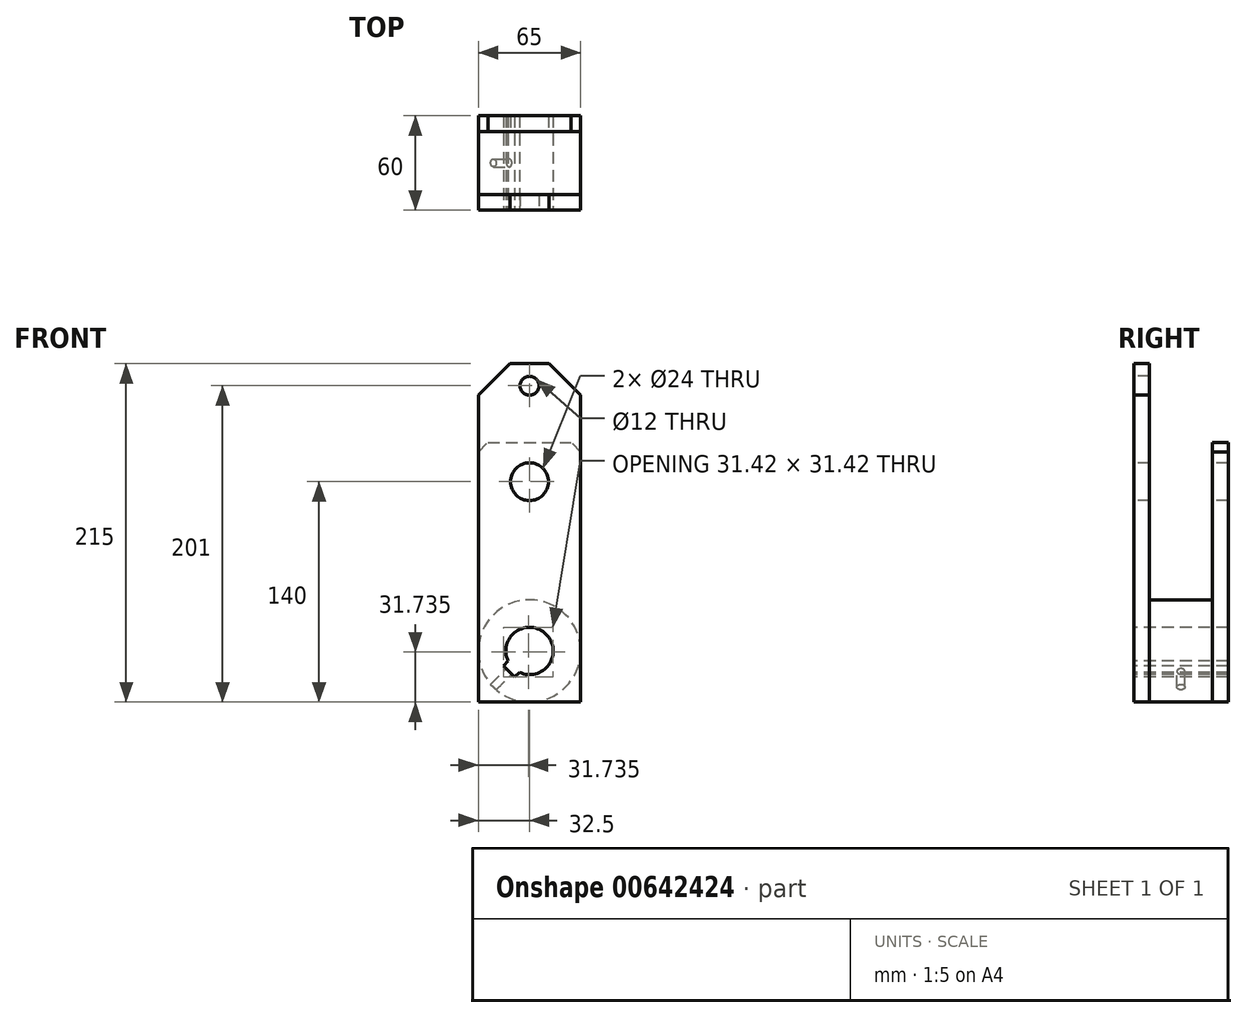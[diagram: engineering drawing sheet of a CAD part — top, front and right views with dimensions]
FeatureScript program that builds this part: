
annotation { "Feature Type Name" : "Feature", "Feature Type Description" : "" }
export const myFeature = defineFeature(function(context is Context, id is Id, definition is map)
    precondition{}
    {
        {
            var Q0;
            Q0=qCreatedBy(makeId("Front.planeOp"),FACE);
            var sketch = newSketch(context, id + "F0", { "sketchPlane" : qUnion([Q0])});
            skLineSegment(sketch, "E0.bottom", {"start": v(32.5, 107.5) * mm, "end": v(-32.5, 107.5) * mm});
            skLineSegment(sketch, "E0.top", {"start": v(32.5, -107.5) * mm, "end": v(-32.5, -107.5) * mm});
            skLineSegment(sketch, "E0.left", {"start": v(32.5, 107.5) * mm, "end": v(32.5, -107.5) * mm});
            skLineSegment(sketch, "E0.right", {"start": v(-32.5, 107.5) * mm, "end": v(-32.5, -107.5) * mm});
            skPoint(sketch, "E0.middle", {"position": v(0, 0) * mm});
            skPoint(sketch, "E1", {"position": v(0, -75) * mm});
            skSolve(sketch);
        }
        {
            var Q0;
            Q0=makeQuery(id+"F0.imprint","IMPRINT",FACE,{"disambiguationData":[TD([[makeQuery(id+"F0.imprint","IMPRINT",EDGE,{"derivedFrom":sQuery(id+"F0.wireOp",EDGE,"E0.bottom")}),1.0]])]});
            extrude(context, id + "F1", {"entities" : qUnion([Q0]), "oppositeDirection" : true, "depth" : 10 * mm, "offsetDistance" : 25 * mm});
        }
        {
            var Q0;
            Q0=makeQuery(id+"F1.opExtrude","SWEPT_EDGE",EDGE,{"disambiguationData":[OSD([sQuery(id+"F0.wireOp",EDGE,"E0.bottom"),sQuery(id+"F0.wireOp",EDGE,"E0.right")])]});
            var Q1;
            Q1=makeQuery(id+"F1.opExtrude","SWEPT_EDGE",EDGE,{"disambiguationData":[OSD([sQuery(id+"F0.wireOp",EDGE,"E0.bottom"),sQuery(id+"F0.wireOp",EDGE,"E0.left")])]});
            chamfer(context, id + "F2", {"entities" : qUnion([Q0, Q1]), "width" : 20 * mm, "tangentPropagation" : true});
        }
        {
            var Q0;
            Q0=makeQuery(id+"F1.opExtrude","CAP_FACE",FACE,{"disambiguationData":[OSD([sQuery(id+"F0.wireOp",EDGE,"E0.bottom"),sQuery(id+"F0.wireOp",EDGE,"E0.top"),sQuery(id+"F0.wireOp",EDGE,"E0.left"),sQuery(id+"F0.wireOp",EDGE,"E0.right")])],"isStart":false});
            var sketch = newSketch(context, id + "F3", { "sketchPlane" : qUnion([Q0])});
            skCircle(sketch, "E2", {"center": v(0, -75) * mm, "radius": 32.5 * mm});
            skSolve(sketch);
        }
        {
            var Q0;
            {var subQ0=sQuery(id+"F3.wireOp",EDGE,"E2");var subQ1=makeQuery(id+"F3.imprint","INTERSECT",VERTEX,{"derivedFrom":[makeQuery(id+"F1.opExtrude","CAP_EDGE",EDGE,{"disambiguationData":[OSD([sQuery(id+"F0.wireOp",EDGE,"E0.left")])],"isStart":false}),subQ0]});Q0=makeQuery(id+"F3.imprint","IMPRINT",FACE,{"disambiguationData":[TD([[makeQuery(id+"F3.imprint","IMPRINT",EDGE,{"disambiguationData":[TD([[subQ1,1.0]])],"derivedFrom":subQ0}),1.0]])]});}
            extrude(context, id + "F4", {"entities" : qUnion([Q0]), "operationType" : NewBodyOperationType.ADD, "depth" : 40 * mm, "offsetDistance" : 25 * mm});
        }
        {
            var Q0;
            Q0=makeQuery(id+"F4.opExtrude","CAP_FACE",FACE,{"disambiguationData":[OSD([sQuery(id+"F3.wireOp",EDGE,"E2")])],"isStart":false});
            var sketch = newSketch(context, id + "F5", { "sketchPlane" : qUnion([Q0])});
            skLineSegment(sketch, "E3.bottom", {"start": v(32.5, -107.5) * mm, "end": v(-32.5, -107.5) * mm});
            skLineSegment(sketch, "E3.top", {"start": v(32.5, 57.5) * mm, "end": v(-32.5, 57.5) * mm});
            skLineSegment(sketch, "E3.left", {"start": v(32.5, -107.5) * mm, "end": v(32.5, 57.5) * mm});
            skLineSegment(sketch, "E3.right", {"start": v(-32.5, -107.5) * mm, "end": v(-32.5, 57.5) * mm});
            skPoint(sketch, "E3.middle", {"position": v(0, -25) * mm});
            skSolve(sketch);
        }
        {
            var Q0;
            {var subQ0=sQuery(id+"F5.wireOp",EDGE,"E3.top");Q0=makeQuery(id+"F5.imprint","IMPRINT",FACE,{"disambiguationData":[TD([[makeQuery(id+"F5.imprint","IMPRINT",EDGE,{"derivedFrom":subQ0}),1.0]])]});}
            var Q1;
            {var subQ0=makeQuery(id+"F4.opExtrude","CAP_EDGE",EDGE,{"disambiguationData":[OSD([sQuery(id+"F3.wireOp",EDGE,"E2")])],"isStart":false});var subQ1=makeQuery(id+"F5.imprint","INTERSECT",VERTEX,{"derivedFrom":[subQ0,sQuery(id+"F5.wireOp",EDGE,"E3.bottom")]});Q1=makeQuery(id+"F5.imprint","IMPRINT",FACE,{"disambiguationData":[TD([[makeQuery(id+"F5.imprint","IMPRINT",EDGE,{"disambiguationData":[TD([[subQ1,-1.0]])],"derivedFrom":subQ0}),1.0]])]});}
            var Q2;
            {var subQ0=sQuery(id+"F5.wireOp",EDGE,"E3.right");var subQ1=sQuery(id+"F5.wireOp",EDGE,"E3.bottom");var subQ2=makeQuery(id+"F5.imprint","INTERSECT",VERTEX,{"derivedFrom":[subQ1,subQ0]});Q2=makeQuery(id+"F5.imprint","IMPRINT",FACE,{"disambiguationData":[TD([[makeQuery(id+"F5.imprint","IMPRINT",EDGE,{"disambiguationData":[TD([[subQ2,1.0]])],"derivedFrom":subQ1}),-1.0]])]});}
            var Q3;
            {var subQ0=sQuery(id+"F5.wireOp",EDGE,"E3.left");var subQ1=sQuery(id+"F5.wireOp",EDGE,"E3.bottom");var subQ2=makeQuery(id+"F5.imprint","INTERSECT",VERTEX,{"derivedFrom":[subQ1,subQ0]});Q3=makeQuery(id+"F5.imprint","IMPRINT",FACE,{"disambiguationData":[TD([[makeQuery(id+"F5.imprint","IMPRINT",EDGE,{"disambiguationData":[TD([[subQ2,-1.0]])],"derivedFrom":subQ1}),-1.0]])]});}
            extrude(context, id + "F6", {"entities" : qUnion([Q0, Q1, Q2, Q3]), "operationType" : NewBodyOperationType.ADD, "depth" : 10 * mm, "offsetDistance" : 25 * mm});
        }
        {
            var Q0;
            Q0=makeQuery(id+"F6.opExtrude","SWEPT_EDGE",EDGE,{"disambiguationData":[OSD([sQuery(id+"F5.wireOp",EDGE,"E3.top"),sQuery(id+"F5.wireOp",EDGE,"E3.right")])]});
            var Q1;
            Q1=makeQuery(id+"F6.opExtrude","SWEPT_EDGE",EDGE,{"disambiguationData":[OSD([sQuery(id+"F5.wireOp",EDGE,"E3.top"),sQuery(id+"F5.wireOp",EDGE,"E3.left")])]});
            chamfer(context, id + "F7", {"entities" : qUnion([Q0, Q1]), "width" : 6 * mm, "tangentPropagation" : true});
        }
        {
            var Q0;
            Q0=makeQuery(id+"F1.opExtrude","CAP_FACE",FACE,{"disambiguationData":[OSD([sQuery(id+"F0.wireOp",EDGE,"E0.bottom"),sQuery(id+"F0.wireOp",EDGE,"E0.top"),sQuery(id+"F0.wireOp",EDGE,"E0.left"),sQuery(id+"F0.wireOp",EDGE,"E0.right")])],"isStart":true});
            var sketch = newSketch(context, id + "F8", { "sketchPlane" : qUnion([Q0])});
            skPoint(sketch, "E4", {"position": v(0, -75) * mm});
            skPoint(sketch, "E5", {"position": v(0, 32.5) * mm});
            skSolve(sketch);
        }
        {
            var Q0;
            Q0=sQuery(id+"F8.wireOp",VERTEX,"E4");
            var Q1;
            Q1=makeQuery(id+"F1.opExtrude","SWEPT_BODY",BODY,{"disambiguationData":[OSD([sQuery(id+"F0.wireOp",EDGE,"E0.bottom"),sQuery(id+"F0.wireOp",EDGE,"E0.top"),sQuery(id+"F0.wireOp",EDGE,"E0.left"),sQuery(id+"F0.wireOp",EDGE,"E0.right")])]});
            hole(context, id + "F9", {"style" : HoleStyle.SIMPLE, "endStyle" : HoleEndStyle.THROUGH, "standardTappedOrClearance" : lookupTablePath({ "standard" : "ISO", "size" : "30", "type" : "Drilled" }), "standardBlindInLast" : lookupTablePath({ "standard" : "ISO", "size" : "30", "type" : "Drilled" }), "holeDiameter" : 30 * mm, "majorDiameter" : 5 * mm, "isTappedThrough" : true, "tappedDepth" : 12 * mm, "tapClearance" : 3, "locations" : qUnion([Q0]), "scope" : qUnion([Q1])});
        }
        {
            var Q0;
            Q0=sQuery(id+"F8.wireOp",VERTEX,"E5");
            var Q1;
            Q1=makeQuery(id+"F1.opExtrude","SWEPT_BODY",BODY,{"disambiguationData":[OSD([sQuery(id+"F0.wireOp",EDGE,"E0.bottom"),sQuery(id+"F0.wireOp",EDGE,"E0.top"),sQuery(id+"F0.wireOp",EDGE,"E0.left"),sQuery(id+"F0.wireOp",EDGE,"E0.right")])]});
            hole(context, id + "F10", {"style" : HoleStyle.SIMPLE, "endStyle" : HoleEndStyle.THROUGH, "standardTappedOrClearance" : lookupTablePath({ "standard" : "ISO", "size" : "24", "type" : "Drilled" }), "standardBlindInLast" : lookupTablePath({ "standard" : "ISO", "size" : "24", "type" : "Drilled" }), "holeDiameter" : 24 * mm, "majorDiameter" : 5 * mm, "isTappedThrough" : true, "tappedDepth" : 12 * mm, "tapClearance" : 3, "locations" : qUnion([Q0]), "scope" : qUnion([Q1])});
        }
        {
            var Q0;
            {var subQ3=sQuery(id+"F0.wireOp",EDGE,"E0.top");Q0=makeQuery(id+"F8.imprint","IMPRINT",FACE,{"disambiguationData":[TD([[makeQuery(id+"F8.imprint","IMPRINT",EDGE,{"derivedFrom":makeQuery(id+"F1.opExtrude","CAP_EDGE",EDGE,{"disambiguationData":[OSD([subQ3])],"isStart":true})}),-1.0]])]});}
            var sketch = newSketch(context, id + "F11", { "sketchPlane" : qUnion([Q0])});
            skArc(sketch, "E6.0", {"start": v(-13.54, -81.46) * mm, "mid": v(-10.6, -85.6) * mm, "end": v(-6.46, -88.54) * mm});
            skLineSegment(sketch, "E7.0", {"start": v(-13.54, -81.46) * mm, "end": v(-16.48, -84.4) * mm});
            skLineSegment(sketch, "E8.0", {"start": v(-6.46, -88.54) * mm, "end": v(-9.4, -91.48) * mm});
            skLineSegment(sketch, "E9", {"start": v(-9.4, -91.48) * mm, "end": v(-16.48, -84.4) * mm});
            skLineSegment(sketch, "E10", {"start": v(0, -75) * mm, "end": v(-12.94, -87.94) * mm, "construction": true});
            skSolve(sketch);
        }
        {
            var Q0;
            Q0=makeQuery(id+"F11.imprint","IMPRINT",FACE,{"disambiguationData":[TD([[makeQuery(id+"F11.imprint","IMPRINT",EDGE,{"derivedFrom":sQuery(id+"F11.wireOp",EDGE,"E6.0")}),-1.0]])]});
            extrude(context, id + "F12", {"entities" : qUnion([Q0]), "operationType" : NewBodyOperationType.REMOVE, "endBound" : BoundingType.THROUGH_ALL, "oppositeDirection" : true, "depth" : 25 * mm, "offsetDistance" : 25 * mm});
        }
        {
            var Q0;
            {var subQ3=sQuery(id+"F0.wireOp",EDGE,"E0.top");Q0=makeQuery(id+"F8.imprint","IMPRINT",FACE,{"disambiguationData":[TD([[makeQuery(id+"F8.imprint","IMPRINT",EDGE,{"derivedFrom":makeQuery(id+"F1.opExtrude","CAP_EDGE",EDGE,{"disambiguationData":[OSD([subQ3])],"isStart":true})}),-1.0]])]});}
            var sketch = newSketch(context, id + "F13", { "sketchPlane" : qUnion([Q0])});
            skCircle(sketch, "E11", {"center": v(0, 93.5) * mm, "radius": 6 * mm});
            skSolve(sketch);
        }
        {
            var Q0;
            Q0=makeQuery(id+"F13.imprint","IMPRINT",FACE,{"disambiguationData":[TD([[makeQuery(id+"F13.imprint","IMPRINT",EDGE,{"derivedFrom":sQuery(id+"F13.wireOp",EDGE,"E11")}),1.0]])]});
            extrude(context, id + "F14", {"entities" : qUnion([Q0]), "operationType" : NewBodyOperationType.REMOVE, "endBound" : BoundingType.UP_TO_NEXT, "oppositeDirection" : true, "depth" : 25 * mm, "offsetDistance" : 25 * mm});
        }
        {
            var Q0;
            Q0=makeQuery(id+"F12.boolean.opBoolean","INTERSECT",VERTEX,{"derivedFrom":[makeQuery(id+"F6.opExtrude","CAP_FACE",FACE,{"disambiguationData":[OSD([sQuery(id+"F5.wireOp",EDGE,"E3.bottom"),sQuery(id+"F5.wireOp",EDGE,"E3.top"),sQuery(id+"F5.wireOp",EDGE,"E3.left"),sQuery(id+"F5.wireOp",EDGE,"E3.right")])],"isStart":false}),makeQuery(id+"F12.opExtrude","SWEPT_FACE",FACE,{"disambiguationData":[OSD([sQuery(id+"F11.wireOp",EDGE,"E7.0")])]}),makeQuery(id+"F12.opExtrude","SWEPT_FACE",FACE,{"disambiguationData":[OSD([sQuery(id+"F11.wireOp",EDGE,"E9")])]})]});
            var Q1;
            Q1=makeQuery(id+"F12.boolean.opBoolean","COPY",VERTEX,{"derivedFrom":makeQuery(id+"F12.opExtrude","CAP_VERTEX",VERTEX,{"disambiguationData":[OSD([sQuery(id+"F11.wireOp",EDGE,"E7.0"),sQuery(id+"F11.wireOp",EDGE,"E9")])],"isStart":true})});
            var Q2;
            Q2=makeQuery(id+"F12.boolean.opBoolean","COPY",VERTEX,{"derivedFrom":makeQuery(id+"F12.opExtrude","CAP_VERTEX",VERTEX,{"disambiguationData":[OSD([sQuery(id+"F11.wireOp",EDGE,"E8.0"),sQuery(id+"F11.wireOp",EDGE,"E9")])],"isStart":true})});
            cPlane(context, id + "F15", {"entities" : qUnion([Q0, Q1, Q2]), "cplaneType" : CPlaneType.THREE_POINT, "offset" : 25 * mm, "width" : 150 * mm, "height" : 150 * mm});
        }
        {
            var Q0;
            Q0=qCreatedBy(id+"F15.planeOp",FACE);
            var sketch = newSketch(context, id + "F16", { "sketchPlane" : qUnion([Q0])});
            skLineSegment(sketch, "E12.0", {"start": v(-60, -48.03) * mm, "end": v(0, -48.03) * mm});
            skPoint(sketch, "E13.0", {"position": v(0, -53.03) * mm});
            skPoint(sketch, "E14", {"position": v(-30, -53.03) * mm});
            skPoint(sketch, "E14.positionSnap0", {"position": v(-30, -48.03) * mm});
            skSolve(sketch);
        }
        {
            var Q0;
            Q0=sQuery(id+"F16.wireOp",VERTEX,"E14");
            var Q1;
            Q1=makeQuery(id+"F1.opExtrude","SWEPT_BODY",BODY,{"disambiguationData":[OSD([sQuery(id+"F0.wireOp",EDGE,"E0.bottom"),sQuery(id+"F0.wireOp",EDGE,"E0.top"),sQuery(id+"F0.wireOp",EDGE,"E0.left"),sQuery(id+"F0.wireOp",EDGE,"E0.right")])]});
            hole(context, id + "F17", {"style" : HoleStyle.SIMPLE, "endStyle" : HoleEndStyle.THROUGH, "oppositeDirection" : true, "standardTappedOrClearance" : lookupTablePath({ "standard" : "ISO", "engagement" : "75%", "pitch" : "1 mm", "size" : "M6", "type" : "Tapped" }), "standardBlindInLast" : lookupTablePath({ "standard" : "ISO", "engagement" : "75%", "pitch" : "1 mm", "size" : "M6", "type" : "Tapped" }), "holeDiameter" : 5 * mm, "majorDiameter" : 6 * mm, "showTappedDepth" : true, "isTappedThrough" : true, "tappedDepth" : 36.5 * mm, "tapClearance" : 2, "locations" : qUnion([Q0]), "scope" : qUnion([Q1])});
        }
    });
